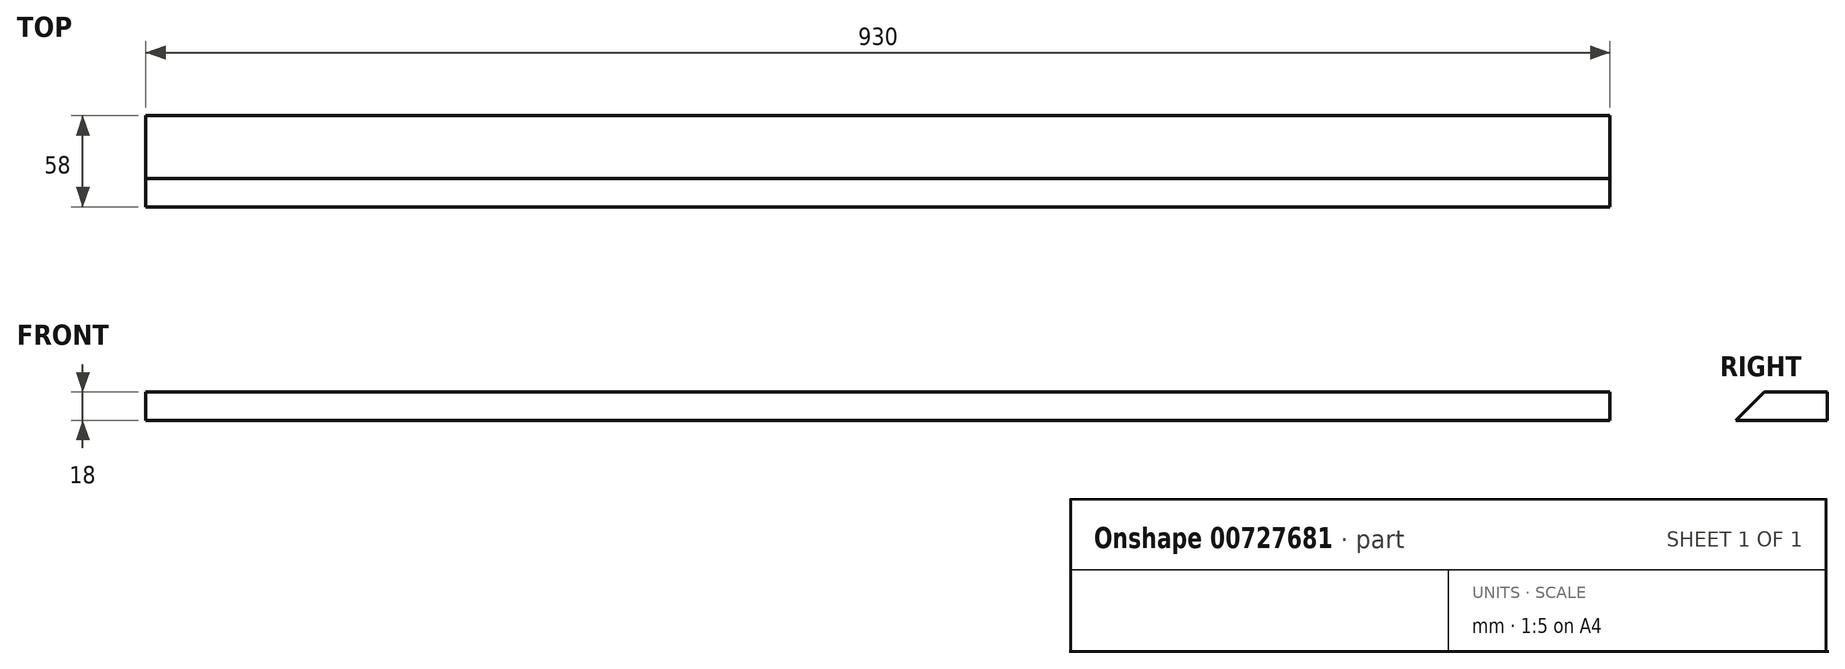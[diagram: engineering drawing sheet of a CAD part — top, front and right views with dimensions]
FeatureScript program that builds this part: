
annotation { "Feature Type Name" : "Feature", "Feature Type Description" : "" }
export const myFeature = defineFeature(function(context is Context, id is Id, definition is map)
    precondition{}
    {
        {
            var Q0;
            Q0=qCreatedBy(makeId("Top.planeOp"),FACE);
            var sketch = newSketch(context, id + "F0", { "sketchPlane" : qUnion([Q0])});
            skLineSegment(sketch, "E0.bottom", {"start": v(-465, -29) * mm, "end": v(465, -29) * mm});
            skLineSegment(sketch, "E0.top", {"start": v(-465, 29) * mm, "end": v(465, 29) * mm});
            skLineSegment(sketch, "E0.left", {"start": v(-465, -29) * mm, "end": v(-465, 29) * mm});
            skLineSegment(sketch, "E0.right", {"start": v(465, -29) * mm, "end": v(465, 29) * mm});
            skPoint(sketch, "E0.middle", {"position": v(0, 0) * mm});
            skSolve(sketch);
        }
        {
            var Q0;
            Q0 = qSketchRegion(id + "F0", true);
            extrude(context, id + "F1", {"entities" : qUnion([Q0]), "depth" : 18 * mm, "offsetDistance" : 25 * mm});
        }
        {
            var Q0;
            Q0=makeQuery(id+"F1.opExtrude","CAP_EDGE",EDGE,{"disambiguationData":[OSD([sQuery(id+"F0.wireOp",EDGE,"E0.bottom")])],"isStart":false});
            chamfer(context, id + "F2", {"entities" : qUnion([Q0]), "width" : 18 * mm, "tangentPropagation" : true});
        }
    });
